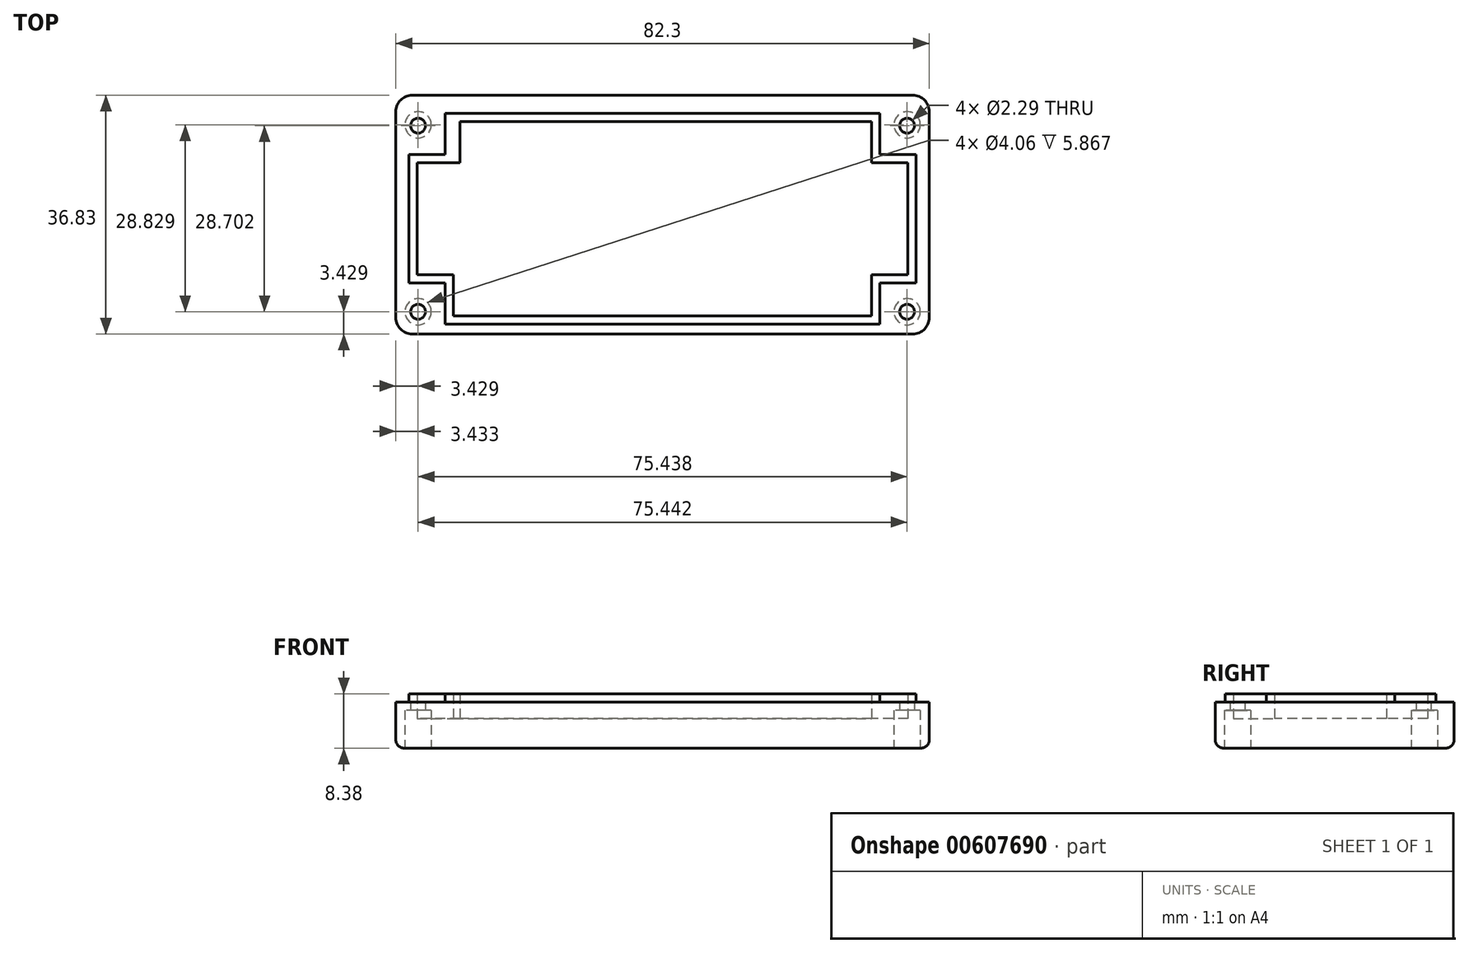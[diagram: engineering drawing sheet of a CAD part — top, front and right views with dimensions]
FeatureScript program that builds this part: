
annotation { "Feature Type Name" : "Feature", "Feature Type Description" : "" }
export const myFeature = defineFeature(function(context is Context, id is Id, definition is map)
    precondition{}
    {
        {
            var Q0;
            Q0=qCreatedBy(makeId("Top.planeOp"),FACE);
            var sketch = newSketch(context, id + "F0", { "sketchPlane" : qUnion([Q0])});
            skLineSegment(sketch, "E0", {"start": v(0, 2.54) * mm, "end": v(0, 34.3) * mm});
            skLineSegment(sketch, "E1", {"start": v(-2.54, 36.83) * mm, "end": v(-79.76, 36.83) * mm});
            skLineSegment(sketch, "E2", {"start": v(-82.3, 34.3) * mm, "end": v(-82.3, 2.54) * mm});
            skLineSegment(sketch, "E3", {"start": v(-79.76, 0) * mm, "end": v(-2.54, 0) * mm});
            skLineSegment(sketch, "E4", {"start": v(-7.62, 1.52) * mm, "end": v(-7.62, 7.87) * mm});
            skLineSegment(sketch, "E5", {"start": v(-7.62, 7.87) * mm, "end": v(-2.03, 7.87) * mm});
            skLineSegment(sketch, "E6", {"start": v(-2.03, 7.87) * mm, "end": v(-2.03, 27.69) * mm});
            skLineSegment(sketch, "E7", {"start": v(-2.03, 27.69) * mm, "end": v(-7.62, 27.69) * mm});
            skLineSegment(sketch, "E8", {"start": v(-7.62, 27.69) * mm, "end": v(-7.62, 34.04) * mm});
            skLineSegment(sketch, "E9", {"start": v(-7.62, 34.04) * mm, "end": v(-74.68, 34.04) * mm});
            skLineSegment(sketch, "E10", {"start": v(-74.68, 34.04) * mm, "end": v(-74.68, 27.69) * mm});
            skLineSegment(sketch, "E11", {"start": v(-74.68, 27.69) * mm, "end": v(-80.26, 27.69) * mm});
            skLineSegment(sketch, "E12", {"start": v(-80.26, 27.69) * mm, "end": v(-80.26, 7.87) * mm});
            skLineSegment(sketch, "E13", {"start": v(-80.26, 7.87) * mm, "end": v(-74.68, 7.87) * mm});
            skLineSegment(sketch, "E14", {"start": v(-74.68, 7.87) * mm, "end": v(-74.68, 1.52) * mm});
            skLineSegment(sketch, "E15", {"start": v(-74.68, 1.52) * mm, "end": v(-7.62, 1.52) * mm});
            skLineSegment(sketch, "E16", {"start": v(-8.9, 2.8) * mm, "end": v(-8.9, 9.14) * mm});
            skLineSegment(sketch, "E17", {"start": v(-8.9, 9.14) * mm, "end": v(-3.3, 9.14) * mm});
            skLineSegment(sketch, "E18", {"start": v(-3.3, 9.14) * mm, "end": v(-3.3, 26.42) * mm});
            skLineSegment(sketch, "E19", {"start": v(-3.3, 26.42) * mm, "end": v(-8.89, 26.42) * mm});
            skLineSegment(sketch, "E20", {"start": v(-8.89, 26.42) * mm, "end": v(-8.9, 32.77) * mm});
            skLineSegment(sketch, "E21", {"start": v(-8.9, 32.77) * mm, "end": v(-72.4, 32.77) * mm});
            skLineSegment(sketch, "E22", {"start": v(-72.4, 32.77) * mm, "end": v(-72.4, 26.42) * mm});
            skLineSegment(sketch, "E23", {"start": v(-72.4, 26.42) * mm, "end": v(-79, 26.42) * mm});
            skLineSegment(sketch, "E24", {"start": v(-79, 26.42) * mm, "end": v(-79, 9.14) * mm});
            skLineSegment(sketch, "E25", {"start": v(-79, 9.14) * mm, "end": v(-73.4, 9.14) * mm});
            skLineSegment(sketch, "E26", {"start": v(-73.4, 9.14) * mm, "end": v(-73.4, 2.8) * mm});
            skLineSegment(sketch, "E27", {"start": v(-73.4, 2.8) * mm, "end": v(-8.9, 2.8) * mm});
            skCircle(sketch, "E28", {"center": v(-3.43, 3.43) * mm, "radius": 1.14 * mm});
            skCircle(sketch, "E29.MirrorC", {"center": v(-3.43, 32.13) * mm, "radius": 1.14 * mm});
            skCircle(sketch, "E30.MirrorC", {"center": v(-78.87, 32.13) * mm, "radius": 1.14 * mm});
            skCircle(sketch, "E31.MirrorC", {"center": v(-78.87, 3.43) * mm, "radius": 1.14 * mm});
            skPoint(sketch, "E32.visualSharp", {"position": v(-82.3, 0) * mm});
            skArc(sketch, "E32.filletArc", {"start": v(-82.3, 2.54) * mm, "mid": v(-81.55, 0.74) * mm, "end": v(-79.76, 0) * mm});
            skPoint(sketch, "E33.visualSharp", {"position": v(0, 0) * mm});
            skArc(sketch, "E33.filletArc", {"start": v(-2.54, 0) * mm, "mid": v(-0.74, 0.74) * mm, "end": v(0, 2.54) * mm});
            skPoint(sketch, "E34.visualSharp", {"position": v(0, 36.83) * mm});
            skArc(sketch, "E34.filletArc", {"start": v(0, 34.3) * mm, "mid": v(-0.74, 36.09) * mm, "end": v(-2.54, 36.83) * mm});
            skPoint(sketch, "E35.visualSharp", {"position": v(-82.3, 36.83) * mm});
            skArc(sketch, "E35.filletArc", {"start": v(-79.76, 36.83) * mm, "mid": v(-81.55, 36.09) * mm, "end": v(-82.3, 34.3) * mm});
            skSolve(sketch);
        }
        {
            var Q0;
            Q0=makeQuery(id+"F0.imprint","IMPRINT",FACE,{"disambiguationData":[TD([[makeQuery(id+"F0.imprint","IMPRINT",EDGE,{"derivedFrom":sQuery(id+"F0.wireOp",EDGE,"E0")}),1.0]])]});
            extrude(context, id + "F1", {"entities" : qUnion([Q0]), "depth" : 7.11 * mm, "offsetDistance" : 25.4 * mm});
        }
        {
            var Q0;
            Q0=makeQuery(id+"F0.imprint","IMPRINT",FACE,{"disambiguationData":[TD([[makeQuery(id+"F0.imprint","IMPRINT",EDGE,{"derivedFrom":sQuery(id+"F0.wireOp",EDGE,"E4")}),1.0]])]});
            extrude(context, id + "F2", {"entities" : qUnion([Q0]), "operationType" : NewBodyOperationType.ADD, "depth" : 8.38 * mm, "offsetDistance" : 25.4 * mm});
        }
        {
            var Q0;
            Q0=makeQuery(id+"F0.imprint","IMPRINT",FACE,{"disambiguationData":[TD([[makeQuery(id+"F0.imprint","IMPRINT",EDGE,{"derivedFrom":sQuery(id+"F0.wireOp",EDGE,"E16")}),1.0]])]});
            extrude(context, id + "F3", {"entities" : qUnion([Q0]), "operationType" : NewBodyOperationType.ADD, "depth" : 4.57 * mm, "offsetDistance" : 25.4 * mm});
        }
        {
            var Q0;
            Q0=makeQuery(id+"F0.imprint","IMPRINT",FACE,{"disambiguationData":[TD([[makeQuery(id+"F0.imprint","IMPRINT",EDGE,{"derivedFrom":sQuery(id+"F0.wireOp",EDGE,"E0")}),1.0]])]});
            var sketch = newSketch(context, id + "F4", { "sketchPlane" : qUnion([Q0])});
            skCircle(sketch, "E36", {"center": v(-3.43, 32.26) * mm, "radius": 2.03 * mm});
            skCircle(sketch, "E37", {"center": v(-78.87, 32.26) * mm, "radius": 2.03 * mm});
            skCircle(sketch, "E38", {"center": v(-3.43, 3.43) * mm, "radius": 2.03 * mm});
            skCircle(sketch, "E39", {"center": v(-78.87, 3.43) * mm, "radius": 2.03 * mm});
            skSolve(sketch);
        }
        {
            var Q0;
            Q0 = qSketchRegion(id + "F4", true);
            extrude(context, id + "F5", {"entities" : qUnion([Q0]), "operationType" : NewBodyOperationType.REMOVE, "depth" : 5.87 * mm, "offsetDistance" : 25.4 * mm});
        }
        {
            var Q0;
            Q0=makeQuery(id+"F1.opExtrude","CAP_EDGE",EDGE,{"disambiguationData":[OSD([sQuery(id+"F0.wireOp",EDGE,"E1")])],"isStart":true});
            fillet(context, id + "F6", {"entities" : qUnion([Q0]), "radius" : 1.27 * mm, "tangentPropagation" : true, "allowEdgeOverflow" : false});
        }
    });
